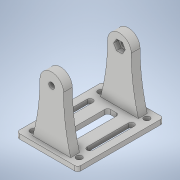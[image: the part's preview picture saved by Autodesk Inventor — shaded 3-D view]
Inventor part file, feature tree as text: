
AUTODESK INVENTOR PART (.ipt)
format: ipt  version: 2020 (Build 240168000, 168)  size: 437,248 bytes
history: native  units: in
note: dims shown in document units (in); Inventor stores cm internally (conversion verified against a paired STEP export)
features: extrude x15, sketch x15, fillet x7, mirror x3, pattern_circular x2, chamfer x2, projected_geometry x1
ambient origin geometry x8: Origin, YZ Plane, XZ Plane, XY Plane, X Axis, Y Axis, Z Axis, Center Point
bodies: Solid1 (feature_tree)
feature tree (45):
  extrude  "Extrusion1"  Depth=0.975in
  extrude  "Extrusion2"  Depth=0.125in TaperAngle=0.0deg
  pattern_circular  "Circular Pattern1"  Count=8 Angle=360.0deg
  extrude  "Extrusion3"  Depth=0.06in TaperAngle=0.0deg
  fillet  "Fillet1"  Radius=0.025in
  extrude  "Extrusion4"  TaperAngle=22.5deg  [1 undecoded]
  pattern_circular  "Circular Pattern2"  Count=8 Angle=360.0deg
  extrude  "Extrusion6"  Depth=0.75in
  extrude  "Extrusion7"  Depth=2.0in
  extrude  "Extrusion9"  Depth=0.125in
  fillet  "Fillet3"  Radius=1.625in
  extrude  "Extrusion10"  Depth=1.25in
  mirror  "Mirror1"
  fillet  "Fillet4"  Radius=2.5in
  chamfer  "Chamfer3"  Distance=2.5in
  chamfer  "Chamfer4"  Distance=0.2165in
  sketch  "Sketch12"  dims[d31=0.5in d32=0.125in d33=1.625in d34=0.0in]
  fillet  "Fillet5"  Radius=0.1in
  fillet  "Fillet6"  Radius=0.0625in
  fillet  "Fillet7"  Radius=1.0in
  extrude  "Extrusion12"  Depth=1.0in TaperAngle=45.0deg
  extrude  "Extrusion13"  Depth=0.25in
  extrude  "Extrusion14"  Depth=0.125in
  extrude  "Extrusion15"  Depth=0.125in
  extrude  "Extrusion17"  Depth=0.125in
  extrude  "Extrusion18"  Depth=1.25in
  mirror  "Mirror2"
  extrude  "Extrusion19"  Depth=0.5in TaperAngle=0.0deg
  mirror  "Mirror3"
  fillet  "Fillet8"  Radius=2.0in
  sketch  "Sketch1"  dims[d0=2.5in d1=0.975in]
  sketch  "Sketch2"  dims[d2=0.125in d3=0.0in d6=0.06in d7=0.0in d8=3.1496in d9=360.0deg]
  projected_geometry  "Projected Loop1"
  sketch  "Sketch3"  dims[d11=0.99in d12=0.06in d13=0.0in d14=0.025in]
  sketch  "Sketch4"  dims[d15=1.1in d16=22.5deg]
  sketch  "Sketch6"  dims[d17=0.125in]
  sketch  "Sketch7"  dims[d18=1.0in d19=0.0in d20=3.1496in d21=360.0deg]
  sketch  "Sketch10"  dims[d23=0.12in d28=0.75in]
  sketch  "Sketch11"  dims[d29=1.5in d30=2.0in]
  sketch  "Sketch13"  dims[d35=2.0in d36=1.25in d37=2.5in d38=0.0in]
  sketch  "Sketch14"  dims[d50=1.5in]
  sketch  "Sketch15"  dims[d51=3.0in]
  sketch  "Sketch17"  dims[d52=0.5in]
  sketch  "Sketch18"  dims[d53=0.5in d54=2.5in d55=0.0in]
  sketch  "Sketch20"  dims[d56=0.25in d57=0.2165in d58=0.1in d59=0.0in d60=0.0625in d61=1.0in d62=0.25in d63=45.0deg d64=1.0in d65=0.25in d66=45.0deg d67=0.25in d70=0.125in d71=0.125in d72=0.125in d73=1.25in d74=2.0in d75=0.0in d76=2.0in d77=0.0in d78=0.175in d79=0.175in d80=0.1in d81=0.0in d82=0.125in d83=1.27in d84=0.0in d94=0.5in d95=1.0in d96=1.0in d97=0.125in d98=0.125in d99=0.125in d100=3.1496in d102=0.125in d103=0.3937in d105=1.0in d107=1.27in d108=0.0in d109=0.075in d110=0.0in d111=0.1in d112=0.0in d113=0.0625in d91=0.5in d92=0.0344in d93=0.5in]
note: 1 required parameter value undecoded (feature->parameter linkage not recoverable at this tier; creation-order binding heuristic only, values carry confidence <= 0.55)
